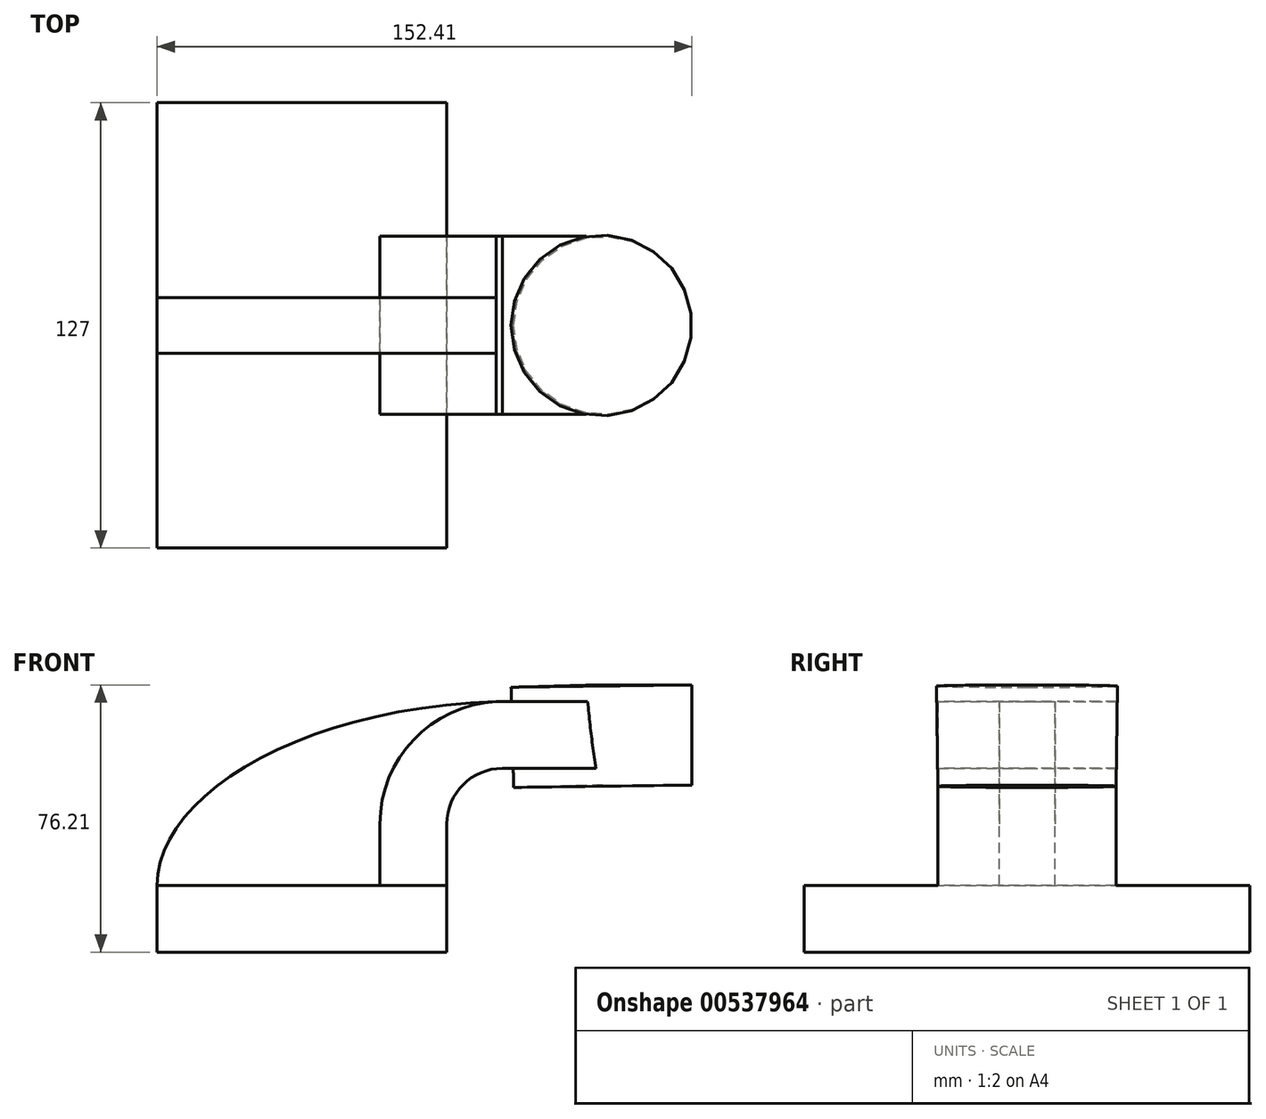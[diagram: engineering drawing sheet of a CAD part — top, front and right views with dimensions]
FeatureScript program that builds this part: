
annotation { "Feature Type Name" : "Feature", "Feature Type Description" : "" }
export const myFeature = defineFeature(function(context is Context, id is Id, definition is map)
    precondition{}
    {
        {
            var Q0;
            Q0=qCreatedBy(makeId("Front.planeOp"),FACE);
            var sketch = newSketch(context, id + "F0", { "sketchPlane" : qUnion([Q0])});
            skLineSegment(sketch, "E0.bottom", {"start": v(41.28, -9.52) * mm, "end": v(-41.28, -9.53) * mm});
            skLineSegment(sketch, "E0.top", {"start": v(41.28, 9.53) * mm, "end": v(-41.28, 9.53) * mm});
            skLineSegment(sketch, "E0.left", {"start": v(41.28, -9.52) * mm, "end": v(41.28, 9.53) * mm});
            skLineSegment(sketch, "E0.right", {"start": v(-41.28, -9.53) * mm, "end": v(-41.28, 9.53) * mm});
            skPoint(sketch, "E0.middle", {"position": v(0, 0) * mm});
            skLineSegment(sketch, "E1.bottom", {"start": v(111.12, 38.1) * mm, "end": v(60.32, 38.1) * mm});
            skLineSegment(sketch, "E1.top", {"start": v(111.12, 66.68) * mm, "end": v(60.32, 66.68) * mm});
            skLineSegment(sketch, "E1.left", {"start": v(111.12, 38.1) * mm, "end": v(111.12, 66.68) * mm});
            skLineSegment(sketch, "E1.right", {"start": v(60.32, 38.1) * mm, "end": v(60.32, 66.68) * mm});
            skPoint(sketch, "E1.middle", {"position": v(85.72, 52.39) * mm});
            skLineSegment(sketch, "E2", {"start": v(41.28, 9.53) * mm, "end": v(41.28, 27) * mm});
            skArc(sketch, "E3", {"start": v(41.27, 27) * mm, "mid": v(45.92, 38.23) * mm, "end": v(57.15, 42.88) * mm});
            skLineSegment(sketch, "E4", {"start": v(57.15, 42.88) * mm, "end": v(85.35, 42.88) * mm});
            skLineSegment(sketch, "E5.0", {"start": v(57.15, 61.93) * mm, "end": v(85.35, 61.93) * mm});
            skArc(sketch, "E5.1", {"start": v(22.23, 27) * mm, "mid": v(32.45, 51.7) * mm, "end": v(57.15, 61.93) * mm});
            skLineSegment(sketch, "E5.2", {"start": v(22.22, 9.53) * mm, "end": v(22.22, 27) * mm});
            skLineSegment(sketch, "E6", {"start": v(85.72, 38.1) * mm, "end": v(85.35, 66.68) * mm});
            skFitSpline(sketch, "E7", {"points": [v(-41.28, 9.53) * mm, v(57.15, 61.93) * mm], "startDerivative": vector(-0.35, 76.24) * mm, "endDerivative": vector(171.45, 3.63) * mm});
            skLineSegment(sketch, "E8.left", {"start": v(57.15, 61.93) * mm, "end": v(57.15, 42.88) * mm});
            skLineSegment(sketch, "E8.right", {"start": v(85.35, 61.93) * mm, "end": v(85.35, 42.88) * mm});
            skSolve(sketch);
        }
        {
            var Q0;
            Q0=makeQuery(id+"F0.imprint","IMPRINT",FACE,{"disambiguationData":[TD([[makeQuery(id+"F0.imprint","IMPRINT",EDGE,{"derivedFrom":sQuery(id+"F0.wireOp",EDGE,"E0.bottom")}),-1.0]])]});
            extrude(context, id + "F1", {"entities" : qUnion([Q0]), "endBound" : BoundingType.SYMMETRIC, "depth" : 127 * mm, "offsetDistance" : 25.4 * mm});
        }
        {
            var Q0;
            {var subQ5=sQuery(id+"F0.wireOp",EDGE,"E2");Q0=makeQuery(id+"F0.imprint","IMPRINT",FACE,{"disambiguationData":[TD([[makeQuery(id+"F0.imprint","IMPRINT",EDGE,{"derivedFrom":subQ5}),1.0]])]});}
            var Q1;
            {var subQ5=sQuery(id+"F0.wireOp",EDGE,"E8.left");Q1=makeQuery(id+"F0.imprint","IMPRINT",FACE,{"disambiguationData":[TD([[makeQuery(id+"F0.imprint","IMPRINT",EDGE,{"derivedFrom":subQ5}),1.0]])]});}
            var Q2;
            {var subQ5=sQuery(id+"F0.wireOp",EDGE,"E8.right");Q2=makeQuery(id+"F0.imprint","IMPRINT",FACE,{"disambiguationData":[TD([[makeQuery(id+"F0.imprint","IMPRINT",EDGE,{"derivedFrom":subQ5}),-1.0]])]});}
            extrude(context, id + "F2", {"entities" : qUnion([Q0, Q1, Q2]), "operationType" : NewBodyOperationType.ADD, "endBound" : BoundingType.SYMMETRIC, "oppositeDirection" : true, "depth" : 50.8 * mm, "offsetDistance" : 25.4 * mm});
        }
        {
            var Q0;
            {var subQ3=sQuery(id+"F0.wireOp",EDGE,"E5.2");Q0=makeQuery(id+"F0.imprint","IMPRINT",FACE,{"disambiguationData":[TD([[makeQuery(id+"F0.imprint","IMPRINT",EDGE,{"derivedFrom":subQ3}),1.0]])]});}
            extrude(context, id + "F3", {"entities" : qUnion([Q0]), "endBound" : BoundingType.SYMMETRIC, "depth" : 15.88 * mm, "offsetDistance" : 25.4 * mm});
        }
        {
            var Q0;
            {var subQ0=sQuery(id+"F0.wireOp",EDGE,"E1.left");Q0=makeQuery(id+"F0.imprint","IMPRINT",FACE,{"disambiguationData":[TD([[makeQuery(id+"F0.imprint","IMPRINT",EDGE,{"derivedFrom":subQ0}),1.0]])]});}
            var Q1;
            Q1=sQuery(id+"F0.wireOp",EDGE,"E6");
            revolve(context, id + "F4", {"operationType" : NewBodyOperationType.ADD, "entities" : qUnion([Q0]), "axis" : qUnion([Q1]), "revolveType" : RevolveType.FULL});
        }
    });
